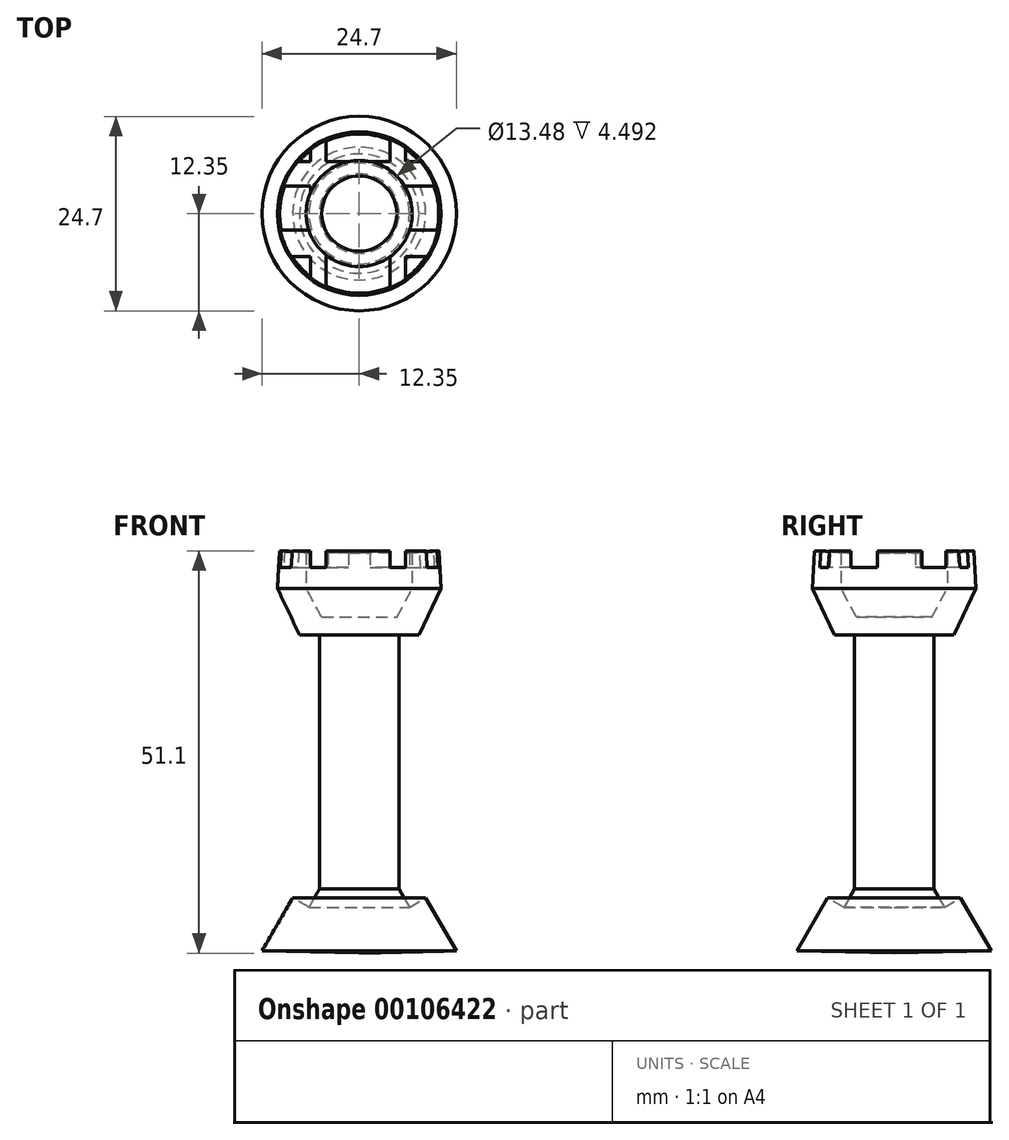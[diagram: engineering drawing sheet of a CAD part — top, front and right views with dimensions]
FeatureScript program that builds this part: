
annotation { "Feature Type Name" : "Feature", "Feature Type Description" : "" }
export const myFeature = defineFeature(function(context is Context, id is Id, definition is map)
    precondition{}
    {
        {
            var Q0;
            Q0=qCreatedBy(makeId("Front.planeOp"),FACE);
            var sketch = newSketch(context, id + "F0", { "sketchPlane" : qUnion([Q0])});
            skLineSegment(sketch, "E0", {"start": v(0, -16.99) * mm, "end": v(0, 25.69) * mm});
            skLineSegment(sketch, "E1", {"start": v(0, 25.69) * mm, "end": v(-4.77, 25.69) * mm});
            skLineSegment(sketch, "E2", {"start": v(-4.77, 25.69) * mm, "end": v(-6.74, 29.34) * mm});
            skLineSegment(sketch, "E3", {"start": v(-6.74, 29.34) * mm, "end": v(-6.74, 33.83) * mm});
            skLineSegment(sketch, "E4", {"start": v(-6.74, 33.83) * mm, "end": v(-10.1, 34.11) * mm});
            skLineSegment(sketch, "E5", {"start": v(-10.1, 34.11) * mm, "end": v(-10.39, 29.34) * mm});
            skLineSegment(sketch, "E6", {"start": v(-10.39, 29.34) * mm, "end": v(-7.58, 23.44) * mm});
            skLineSegment(sketch, "E7", {"start": v(-7.58, 23.44) * mm, "end": v(-5.05, 23.44) * mm});
            skLineSegment(sketch, "E8", {"start": v(-5.05, 23.44) * mm, "end": v(-5.05, -8.84) * mm});
            skLineSegment(sketch, "E9", {"start": v(-5.05, -8.84) * mm, "end": v(-6.39, -11.15) * mm});
            skLineSegment(sketch, "E10", {"start": v(-6.39, -11.15) * mm, "end": v(-8.44, -9.95) * mm});
            skLineSegment(sketch, "E11", {"start": v(-8.44, -9.95) * mm, "end": v(-12.35, -16.7) * mm});
            skLineSegment(sketch, "E12", {"start": v(0, -16.99) * mm, "end": v(-12.35, -16.7) * mm});
            skSolve(sketch);
        }
        {
            var Q0;
            Q0 = qSketchRegion(id + "F0", true);
            var Q1;
            Q1=sQuery(id+"F0.wireOp",EDGE,"E0");
            revolve(context, id + "F1", {"entities" : qUnion([Q0]), "axis" : qUnion([Q1]), "revolveType" : RevolveType.FULL});
        }
        {
            var Q0;
            Q0=qCreatedBy(makeId("Top.planeOp"),FACE);
            cPlane(context, id + "F2", {"entities" : qUnion([Q0]), "cplaneType" : CPlaneType.OFFSET, "offset" : 35 * mm, "width" : 150 * mm, "height" : 150 * mm});
        }
        {
            var Q0;
            Q0=qCreatedBy(id+"F2.planeOp",FACE);
            var sketch = newSketch(context, id + "F3", { "sketchPlane" : qUnion([Q0])});
            skLineSegment(sketch, "E13.bottom", {"start": v(-6.18, 13.34) * mm, "end": v(-4.21, 13.34) * mm});
            skLineSegment(sketch, "E13.top", {"start": v(-6.18, -15.3) * mm, "end": v(-4.21, -15.3) * mm});
            skLineSegment(sketch, "E13.left", {"start": v(-6.18, 13.34) * mm, "end": v(-6.18, -15.3) * mm});
            skLineSegment(sketch, "E13.right", {"start": v(-4.21, 13.34) * mm, "end": v(-4.21, -15.3) * mm});
            skLineSegment(sketch, "E14.bottom", {"start": v(3.93, 10.25) * mm, "end": v(5.9, 10.25) * mm});
            skLineSegment(sketch, "E14.top", {"start": v(3.93, -14.46) * mm, "end": v(5.9, -14.46) * mm});
            skLineSegment(sketch, "E14.left", {"start": v(3.93, 10.25) * mm, "end": v(3.93, -14.46) * mm});
            skLineSegment(sketch, "E14.right", {"start": v(5.9, 10.25) * mm, "end": v(5.9, -14.46) * mm});
            skLineSegment(sketch, "E15.bottom", {"start": v(-13.48, 6.6) * mm, "end": v(14.32, 6.6) * mm});
            skLineSegment(sketch, "E15.top", {"start": v(-13.48, 3.5) * mm, "end": v(14.32, 3.5) * mm});
            skLineSegment(sketch, "E15.left", {"start": v(-13.48, 6.6) * mm, "end": v(-13.48, 3.5) * mm});
            skLineSegment(sketch, "E15.right", {"start": v(14.32, 6.6) * mm, "end": v(14.32, 3.5) * mm});
            skPoint(sketch, "E16.oppositeSnap0", {"position": v(5.9, -2.1) * mm});
            skLineSegment(sketch, "E16.bottom", {"start": v(-12.35, -5.47) * mm, "end": v(13.2, -5.47) * mm});
            skLineSegment(sketch, "E16.top", {"start": v(-12.35, -2.1) * mm, "end": v(13.2, -2.1) * mm});
            skLineSegment(sketch, "E16.left", {"start": v(-12.35, -5.47) * mm, "end": v(-12.35, -2.1) * mm});
            skLineSegment(sketch, "E16.right", {"start": v(13.2, -5.47) * mm, "end": v(13.2, -2.1) * mm});
            skSolve(sketch);
        }
        {
            var Q0;
            Q0 = qSketchRegion(id + "F3", true);
            extrude(context, id + "F4", {"entities" : qUnion([Q0]), "operationType" : NewBodyOperationType.REMOVE, "oppositeDirection" : true, "depth" : 3 * mm});
        }
    });
